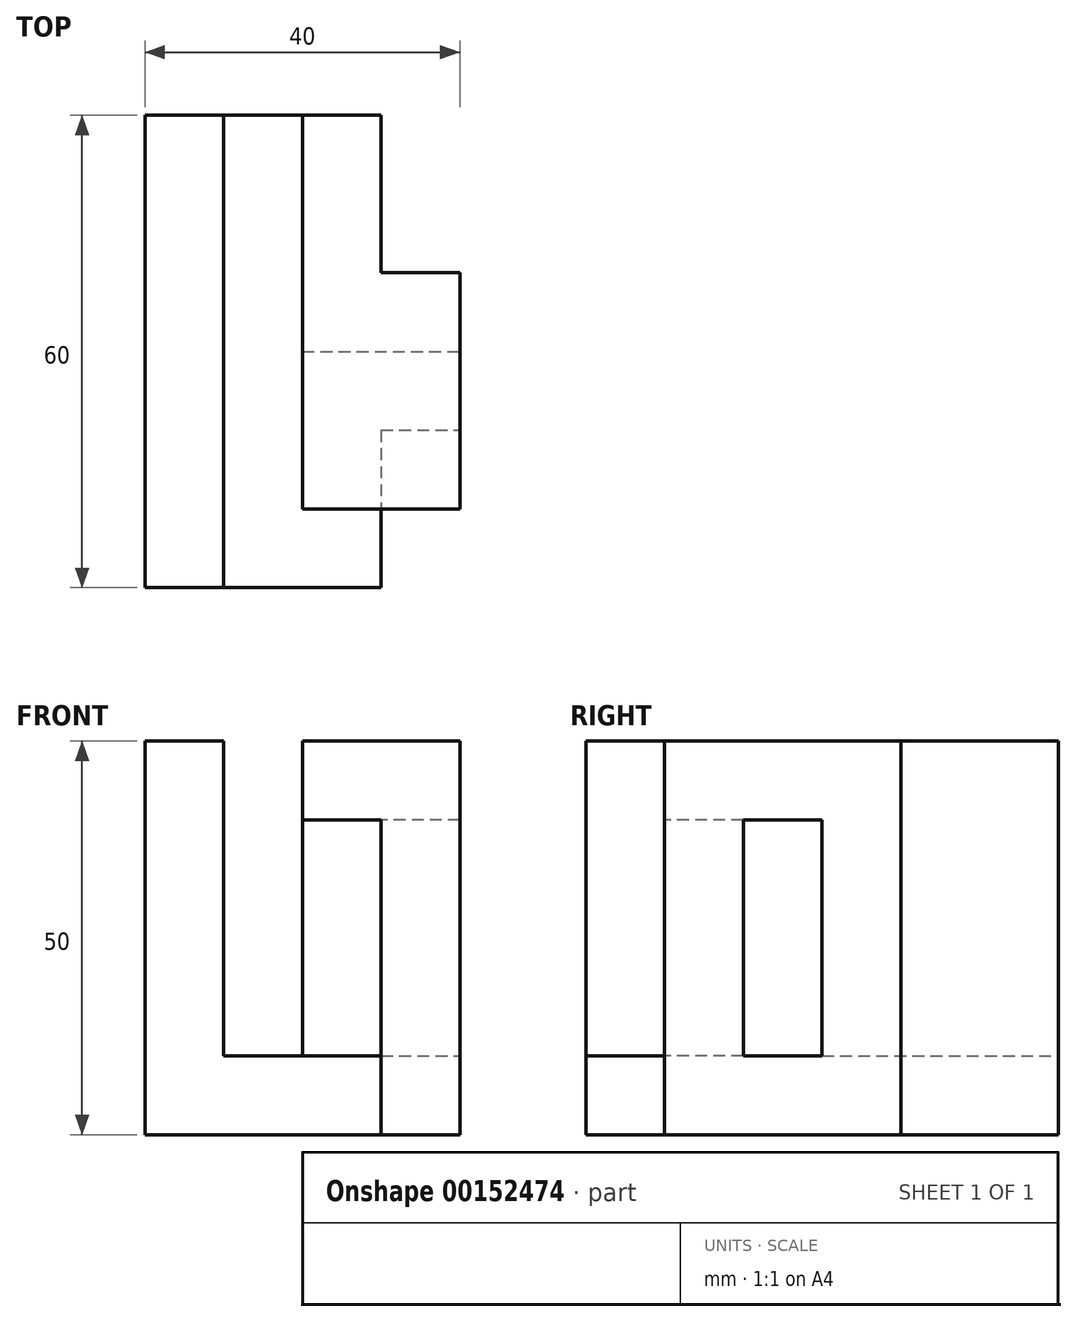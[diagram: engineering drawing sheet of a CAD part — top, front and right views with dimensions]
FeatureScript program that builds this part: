
annotation { "Feature Type Name" : "Feature", "Feature Type Description" : "" }
export const myFeature = defineFeature(function(context is Context, id is Id, definition is map)
    precondition{}
    {
        {
            var Q0;
            Q0=qCreatedBy(makeId("Front.planeOp"),FACE);
            var sketch = newSketch(context, id + "F0", { "sketchPlane" : qUnion([Q0])});
            skLineSegment(sketch, "E0", {"start": v(0, 0) * mm, "end": v(0, 50) * mm});
            skLineSegment(sketch, "E1", {"start": v(0, 50) * mm, "end": v(10, 50) * mm});
            skLineSegment(sketch, "E2", {"start": v(10, 50) * mm, "end": v(10, 10) * mm});
            skLineSegment(sketch, "E3", {"start": v(10, 10) * mm, "end": v(20, 10) * mm});
            skLineSegment(sketch, "E4", {"start": v(20, 10) * mm, "end": v(20, 50) * mm});
            skLineSegment(sketch, "E5", {"start": v(20, 50) * mm, "end": v(30, 50) * mm});
            skLineSegment(sketch, "E6", {"start": v(30, 50) * mm, "end": v(30, 0) * mm});
            skLineSegment(sketch, "E7", {"start": v(30, 0) * mm, "end": v(0, 0) * mm});
            skSolve(sketch);
        }
        {
            var Q0;
            Q0=makeQuery(id+"F0.imprint","IMPRINT",FACE,{"disambiguationData":[TD([[makeQuery(id+"F0.imprint","IMPRINT",EDGE,{"derivedFrom":sQuery(id+"F0.wireOp",EDGE,"E0")}),-1.0]])]});
            extrude(context, id + "F1", {"entities" : qUnion([Q0]), "endBound" : BoundingType.SYMMETRIC, "depth" : 60 * mm});
        }
        {
            var Q0;
            Q0=makeQuery(id+"F1.opExtrude","SWEPT_FACE",FACE,{"disambiguationData":[OSD([sQuery(id+"F0.wireOp",EDGE,"E5")])]});
            var sketch = newSketch(context, id + "F2", { "sketchPlane" : qUnion([Q0])});
            skLineSegment(sketch, "E8.bottom", {"start": v(30, 10) * mm, "end": v(40, 10) * mm});
            skLineSegment(sketch, "E8.top", {"start": v(30, -20) * mm, "end": v(40, -20) * mm});
            skLineSegment(sketch, "E8.left", {"start": v(30, 10) * mm, "end": v(30, -20) * mm});
            skLineSegment(sketch, "E8.right", {"start": v(40, 10) * mm, "end": v(40, -20) * mm});
            skSolve(sketch);
        }
        {
            var Q0;
            Q0=makeQuery(id+"F2.imprint","IMPRINT",FACE,{"disambiguationData":[TD([[makeQuery(id+"F2.imprint","IMPRINT",EDGE,{"derivedFrom":sQuery(id+"F2.wireOp",EDGE,"E8.bottom")}),-1.0]])]});
            var Q1;
            Q1=makeQuery(id+"F1.opExtrude","SWEPT_FACE",FACE,{"disambiguationData":[OSD([sQuery(id+"F0.wireOp",EDGE,"E7")])]});
            extrude(context, id + "F3", {"entities" : qUnion([Q0]), "operationType" : NewBodyOperationType.ADD, "endBound" : BoundingType.UP_TO_SURFACE, "oppositeDirection" : true, "endBoundEntityFace" : qUnion([Q1]), "depth" : 25 * mm});
        }
        {
            var Q0;
            Q0=makeQuery(id+"F1.opExtrude","CAP_FACE",FACE,{"disambiguationData":[OSD([sQuery(id+"F0.wireOp",EDGE,"E0"),sQuery(id+"F0.wireOp",EDGE,"E1"),sQuery(id+"F0.wireOp",EDGE,"E2"),sQuery(id+"F0.wireOp",EDGE,"E3"),sQuery(id+"F0.wireOp",EDGE,"E4"),sQuery(id+"F0.wireOp",EDGE,"E5"),sQuery(id+"F0.wireOp",EDGE,"E6"),sQuery(id+"F0.wireOp",EDGE,"E7")])],"isStart":false});
            var sketch = newSketch(context, id + "F4", { "sketchPlane" : qUnion([Q0])});
            skLineSegment(sketch, "E9", {"start": v(20, 50) * mm, "end": v(40, 50) * mm});
            skLineSegment(sketch, "E10", {"start": v(40, 50) * mm, "end": v(40, 0) * mm});
            skLineSegment(sketch, "E11", {"start": v(40, 0) * mm, "end": v(30, 0) * mm});
            skLineSegment(sketch, "E12", {"start": v(30, 0) * mm, "end": v(30, 40) * mm});
            skLineSegment(sketch, "E13", {"start": v(30, 40) * mm, "end": v(20, 40) * mm});
            skLineSegment(sketch, "E14", {"start": v(20, 40) * mm, "end": v(20, 50) * mm});
            skSolve(sketch);
        }
        {
            var Q0;
            {var subQ4=sQuery(id+"F4.wireOp",EDGE,"E13");Q0=makeQuery(id+"F4.imprint","IMPRINT",FACE,{"disambiguationData":[TD([[makeQuery(id+"F4.imprint","IMPRINT",EDGE,{"derivedFrom":subQ4}),-1.0]])]});}
            var Q1;
            {var subQ4=sQuery(id+"F4.wireOp",EDGE,"E10");Q1=makeQuery(id+"F4.imprint","IMPRINT",FACE,{"disambiguationData":[TD([[makeQuery(id+"F4.imprint","IMPRINT",EDGE,{"derivedFrom":subQ4}),-1.0]])]});}
            extrude(context, id + "F5", {"entities" : qUnion([Q0, Q1]), "operationType" : NewBodyOperationType.REMOVE, "oppositeDirection" : true, "depth" : 10 * mm});
        }
        {
            var Q0;
            Q0=makeQuery(id+"F1.opExtrude","CAP_FACE",FACE,{"disambiguationData":[OSD([sQuery(id+"F0.wireOp",EDGE,"E0"),sQuery(id+"F0.wireOp",EDGE,"E1"),sQuery(id+"F0.wireOp",EDGE,"E2"),sQuery(id+"F0.wireOp",EDGE,"E3"),sQuery(id+"F0.wireOp",EDGE,"E4"),sQuery(id+"F0.wireOp",EDGE,"E5"),sQuery(id+"F0.wireOp",EDGE,"E6"),sQuery(id+"F0.wireOp",EDGE,"E7")])],"isStart":false});
            var sketch = newSketch(context, id + "F6", { "sketchPlane" : qUnion([Q0])});
            skLineSegment(sketch, "E15.bottom", {"start": v(20, 40) * mm, "end": v(30, 40) * mm});
            skLineSegment(sketch, "E15.top", {"start": v(20, 10) * mm, "end": v(30, 10) * mm});
            skLineSegment(sketch, "E15.left", {"start": v(20, 40) * mm, "end": v(20, 10) * mm});
            skLineSegment(sketch, "E15.right", {"start": v(30, 40) * mm, "end": v(30, 10) * mm});
            skSolve(sketch);
        }
        {
            var Q0;
            Q0=makeQuery(id+"F6.imprint","IMPRINT",FACE,{"disambiguationData":[TD([[makeQuery(id+"F6.imprint","IMPRINT",EDGE,{"derivedFrom":sQuery(id+"F6.wireOp",EDGE,"E15.bottom")}),1.0]])]});
            extrude(context, id + "F7", {"entities" : qUnion([Q0]), "operationType" : NewBodyOperationType.REMOVE, "oppositeDirection" : true, "depth" : 30 * mm});
        }
        {
            var Q0;
            Q0=makeQuery(id+"F3.opExtrude","SWEPT_FACE",FACE,{"disambiguationData":[OSD([sQuery(id+"F2.wireOp",EDGE,"E8.right")])]});
            var sketch = newSketch(context, id + "F8", { "sketchPlane" : qUnion([Q0])});
            skLineSegment(sketch, "E16.bottom", {"start": v(-10, 40) * mm, "end": v(0, 40) * mm});
            skLineSegment(sketch, "E16.top", {"start": v(-10, 10) * mm, "end": v(0, 10) * mm});
            skLineSegment(sketch, "E16.left", {"start": v(-10, 40) * mm, "end": v(-10, 10) * mm});
            skLineSegment(sketch, "E16.right", {"start": v(0, 40) * mm, "end": v(0, 10) * mm});
            skSolve(sketch);
        }
        {
            var Q0;
            Q0=makeQuery(id+"F8.imprint","IMPRINT",FACE,{"disambiguationData":[TD([[makeQuery(id+"F8.imprint","IMPRINT",EDGE,{"derivedFrom":sQuery(id+"F8.wireOp",EDGE,"E16.bottom")}),-1.0]])]});
            extrude(context, id + "F9", {"entities" : qUnion([Q0]), "operationType" : NewBodyOperationType.REMOVE, "endBound" : BoundingType.UP_TO_NEXT, "oppositeDirection" : true, "depth" : 25 * mm});
        }
    });
